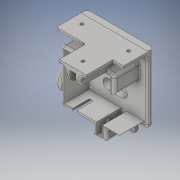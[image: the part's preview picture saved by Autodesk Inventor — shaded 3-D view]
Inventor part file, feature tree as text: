
AUTODESK INVENTOR PART (.ipt)
format: ipt  version: 2016 (Build 200138000, 138)  size: 1,053,184 bytes
history: native  units: in
note: dims shown in document units (in); Inventor stores cm internally (conversion verified against a paired STEP export)
features: sketch x18, plane x4, other x3
ambient origin geometry x8: Origin, YZ Plane, XZ Plane, XY Plane, X Axis, Y Axis, Z Axis, Center Point
bodies: Solid1 (feature_tree)
feature tree (25):
  other  "ankle_holder.ipt"
  other  "Solid1::ankle_holder.ipt"
  other  "TaggingFeature1"
  sketch  "Sketch1"  dims[d0=0.3937in]
  sketch  "Sketch12"
  sketch  "Sketch14"
  sketch  "Sketch17"
  sketch  "Sketch18"
  sketch  "Sketch22"
  sketch  "Sketch24"
  sketch  "Sketch30"
  sketch  "Sketch32"
  sketch  "Sketch33"
  sketch  "Sketch35"
  sketch  "Sketch36"
  sketch  "Sketch37"
  sketch  "Sketch38"
  sketch  "Sketch40"
  sketch  "Sketch41"
  sketch  "Sketch42"
  sketch  "Sketch43"
  plane  "Work Plane1"
  plane  "Work Plane4"
  plane  "Work Plane5"
  plane  "Work Plane6"
